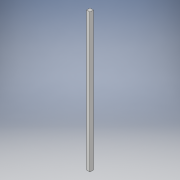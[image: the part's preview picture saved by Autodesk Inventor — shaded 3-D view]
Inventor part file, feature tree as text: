
AUTODESK INVENTOR PART (.ipt)
format: ipt  version: 2019 (Build 230136000, 136)  size: 97,792 bytes
history: native  units: mm
features: other x1, extrude x1, sketch x1
ambient origin geometry x8: Origin, YZ Plane, XZ Plane, XY Plane, X Axis, Y Axis, Z Axis, Center Point
bodies: Body1 (feature_tree)
feature tree (3):
  other  "ソリッド1"
  extrude  "押し出し1"  Depth=10.0mm
  sketch  "スケッチ1"
